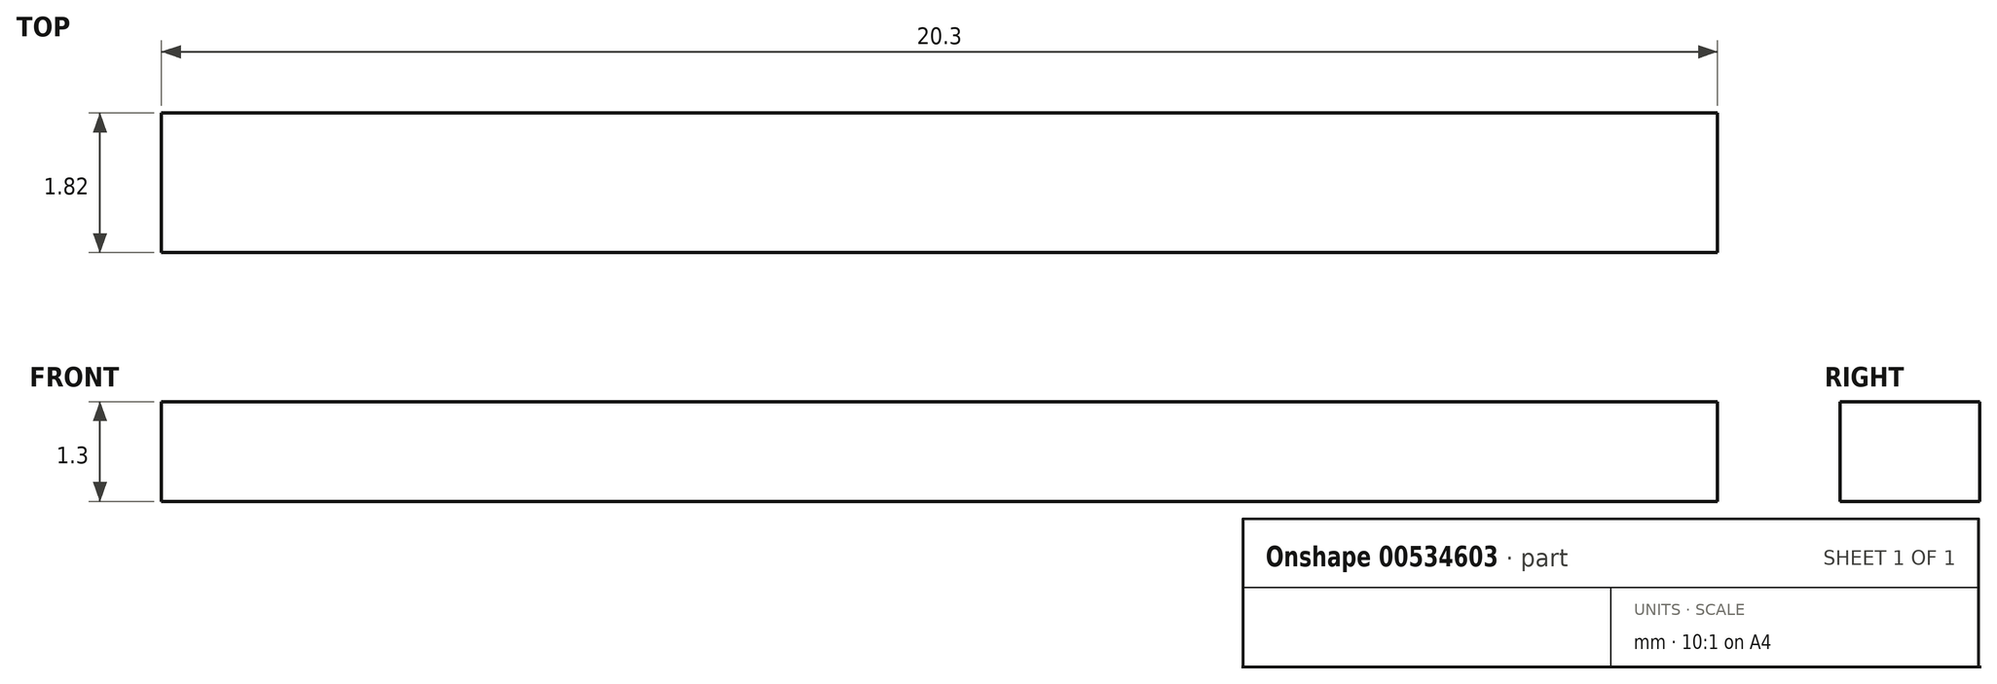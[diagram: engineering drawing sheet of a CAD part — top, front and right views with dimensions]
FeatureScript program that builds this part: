
annotation { "Feature Type Name" : "Feature", "Feature Type Description" : "" }
export const myFeature = defineFeature(function(context is Context, id is Id, definition is map)
    precondition{}
    {
        {
            var Q0;
            Q0=qCreatedBy(makeId("Top.planeOp"),FACE);
            var sketch = newSketch(context, id + "F0", { "sketchPlane" : qUnion([Q0])});
            skLineSegment(sketch, "E0.bottom", {"start": v(10.15, -0.9) * mm, "end": v(-10.15, -0.91) * mm});
            skLineSegment(sketch, "E0.top", {"start": v(10.15, 0.91) * mm, "end": v(-10.15, 0.9) * mm});
            skLineSegment(sketch, "E0.left", {"start": v(10.15, -0.9) * mm, "end": v(10.15, 0.91) * mm});
            skLineSegment(sketch, "E0.right", {"start": v(-10.15, -0.91) * mm, "end": v(-10.15, 0.91) * mm});
            skPoint(sketch, "E0.middle", {"position": v(0, 0) * mm});
            skSolve(sketch);
        }
        {
            var Q0;
            Q0=makeQuery(id+"F0.imprint","IMPRINT",FACE,{"disambiguationData":[TD([[makeQuery(id+"F0.imprint","IMPRINT",EDGE,{"derivedFrom":sQuery(id+"F0.wireOp",EDGE,"E0.bottom")}),-1.0]])]});
            extrude(context, id + "F1", {"entities" : qUnion([Q0]), "depth" : 1.3 * mm, "offsetDistance" : 25 * mm});
        }
    });
